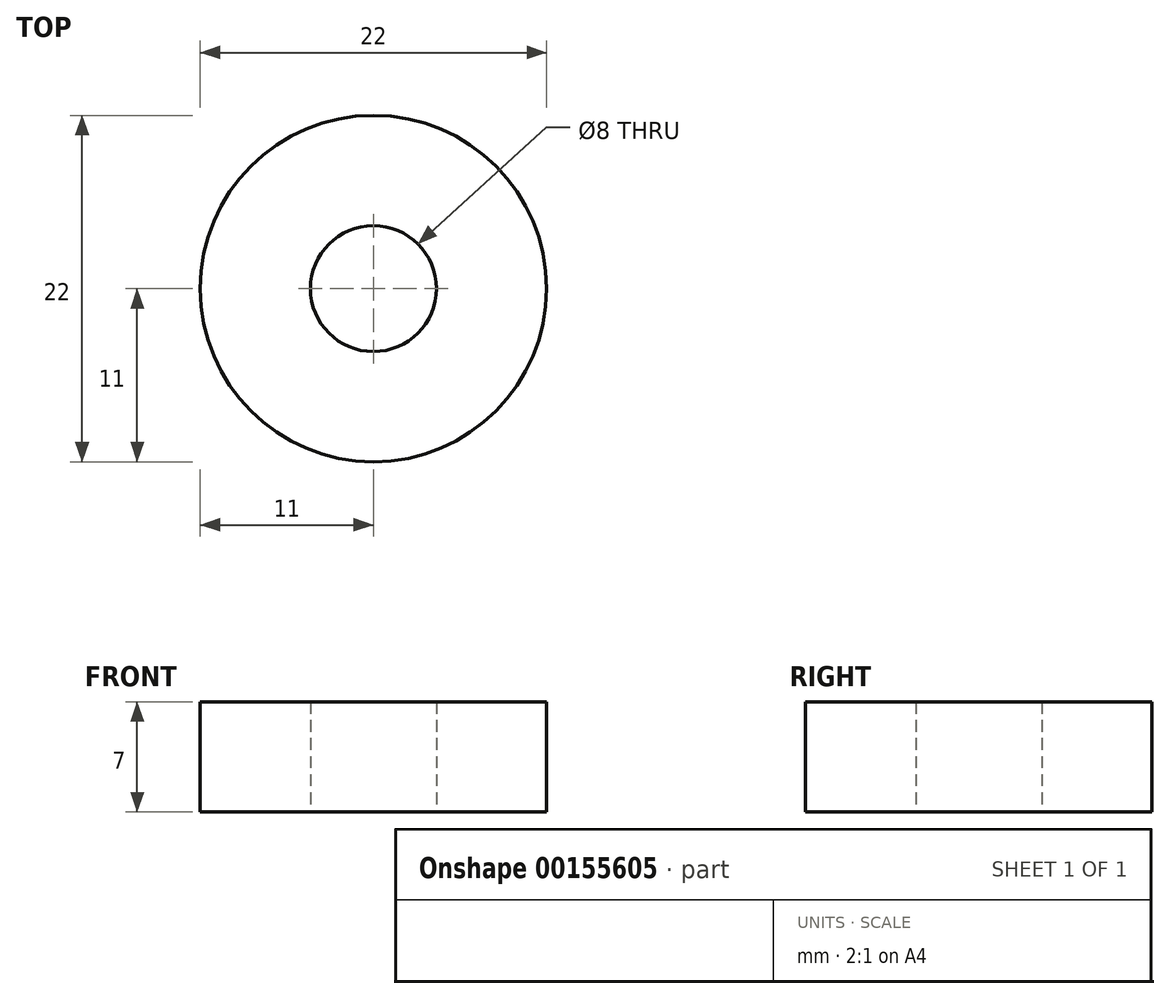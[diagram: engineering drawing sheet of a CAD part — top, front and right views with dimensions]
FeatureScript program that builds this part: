
annotation { "Feature Type Name" : "Feature", "Feature Type Description" : "" }
export const myFeature = defineFeature(function(context is Context, id is Id, definition is map)
    precondition{}
    {
        {
            var Q0;
            Q0=qCreatedBy(makeId("Top.planeOp"),FACE);
            var sketch = newSketch(context, id + "F0", { "sketchPlane" : qUnion([Q0])});
            skCircle(sketch, "E0", {"center": v(0, 0) * mm, "radius": 11 * mm});
            skCircle(sketch, "E1", {"center": v(0, 0) * mm, "radius": 4 * mm});
            skSolve(sketch);
        }
        {
            var Q0;
            Q0=makeQuery(id+"F0.imprint","IMPRINT",FACE,{"disambiguationData":[TD([[makeQuery(id+"F0.imprint","IMPRINT",EDGE,{"derivedFrom":sQuery(id+"F0.wireOp",EDGE,"E0")}),1.0]])]});
            extrude(context, id + "F1", {"entities" : qUnion([Q0]), "depth" : 7 * mm});
        }
    });
